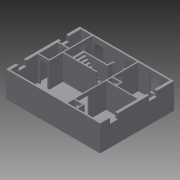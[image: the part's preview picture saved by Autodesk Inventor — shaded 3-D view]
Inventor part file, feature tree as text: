
AUTODESK INVENTOR PART (.ipt)
format: ipt  version: 2013 (Build 170138000, 138)  size: 444,928 bytes
history: native  units: in
note: dims shown in document units (in); Inventor stores cm internally (conversion verified against a paired STEP export)
features: extrude x10, sketch x8, projected_geometry x1
ambient origin geometry x8: Origin, YZ Plane, XZ Plane, XY Plane, X Axis, Y Axis, Z Axis, Center Point
feature tree (19):
  sketch  "Sketch1"  dims[d0=360.0in d3=282.0in]
  extrude  "Extrusion8"  Depth=282.0in
  extrude  "Extrusion9"  Depth=144.0in
  extrude  "Extrusion12"  Depth=66.0in
  extrude  "Extrusion13"  Depth=216.0in
  extrude  "Extrusion14"  Depth=147.0in
  extrude  "Extrusion15"  Depth=4.0in
  extrude  "Extrusion16"  Depth=120.0in
  sketch  "Sketch14"  dims[d21=48.0in d27=4.0in d29=15.0in]
  sketch  "Sketch15"  dims[d31=150.0in d33=66.0in d34=70.0in d35=4.0in d40=120.0in d41=216.0in]
  sketch  "Sketch16"  dims[d46=36.0in d53=4.0in d54=120.0in d55=10.0in d56=10.0in d59=4.5in d60=38.0in d70=30.0in d71=10.0in d72=30.0in d74=18.0in d75=10.0in d76=120.0in d77=117.0in d83=66.0in d85=84.0in d86=66.0in d94=120.0in d95=4.5in d96=4.5in d98=6.0in d148=6.0in d149=10.0in d150=10.0in d151=10.0in d152=10.0in d153=6.0in d154=6.0in d155=282.0in d156=120.0in d157=4.5in d160=6.0in d161=6.0in d163=4.5in d164=120.0in d165=4.5in d167=147.0in d168=118.5in d169=118.5in d170=2.25in d171=27.5in d172=2.25in d173=4.5in d174=6.0in d175=4.5in d176=4.5in d177=24.0in d178=24.0in d179=48.0in d180=4.5in d181=4.5in d182=18.0in d184=18.0in d186=4.5in d188=27.5in d189=2.25in d190=2.25in d191=4.5in d192=2.25in d195=40.0in d196=4.5in d197=4.5in d198=40.0in d199=36.0in d200=30.0in d201=105.0in d202=4.5in d209=4.5in d217=4.5in d225=96.0in d226=0.0in d227=3.0in d228=0.0in d258=30.0in d260=20.0in d261=37.5in d262=30.0in d263=20.0in d264=65.0in d265=10.0in d266=0.0in d267=20.0in d268=30.0in d269=52.0in d270=37.5in d271=30.0in d272=20.0in d273=10.0in d274=0.0in d275=57.0in d277=38.0in d278=58.0in d279=20.0in d280=20.0in d281=49.5in d282=38.0in d283=57.0in d284=10.0in d285=0.0in d289=36.0in d290=4.5in d291=19.0in d292=3.0in d293=4.5in d296=4.5in d297=72.0in d299=4.5in d302=128.0in d303=96.0in d304=4.0in d305=96.0in d306=0.0in d307=96.0in d308=0.0in d311=28.0in d313=8.25in d314=14.0in d317=8.0in d319=8.0in d320=8.0in d321=8.0in d322=8.0in d323=8.0in d324=8.0in d325=8.0in d326=8.0in d327=8.0in d328=8.0in d329=8.0in d330=8.0in d331=8.0in d332=8.0in d333=8.0in d334=8.0in d335=8.0in d336=8.0in d337=8.0in d338=8.0in d339=8.0in d342=4.5in d343=4.5in d344=14.0in d345=0.0in d346=38.0in d347=0.0in d348=4.5in d349=0.0in d350=66.0in]
  extrude  "Extrusion20"  Depth=4.0in
  extrude  "Extrusion21"  Depth=10.0in
  extrude  "Extrusion22"  Depth=4.5in
  sketch  "Sketch8"  dims[d4=340.0in d5=262.0in d8=144.0in]
  sketch  "Sketch11"  dims[d9=180.0in d10=66.0in d11=66.0in]
  sketch  "Sketch12"  dims[d12=4.0in d13=4.5in d17=216.0in]
  sketch  "Sketch13"  dims[d18=4.0in d19=147.0in]
  projected_geometry  "Projected Loop1"
